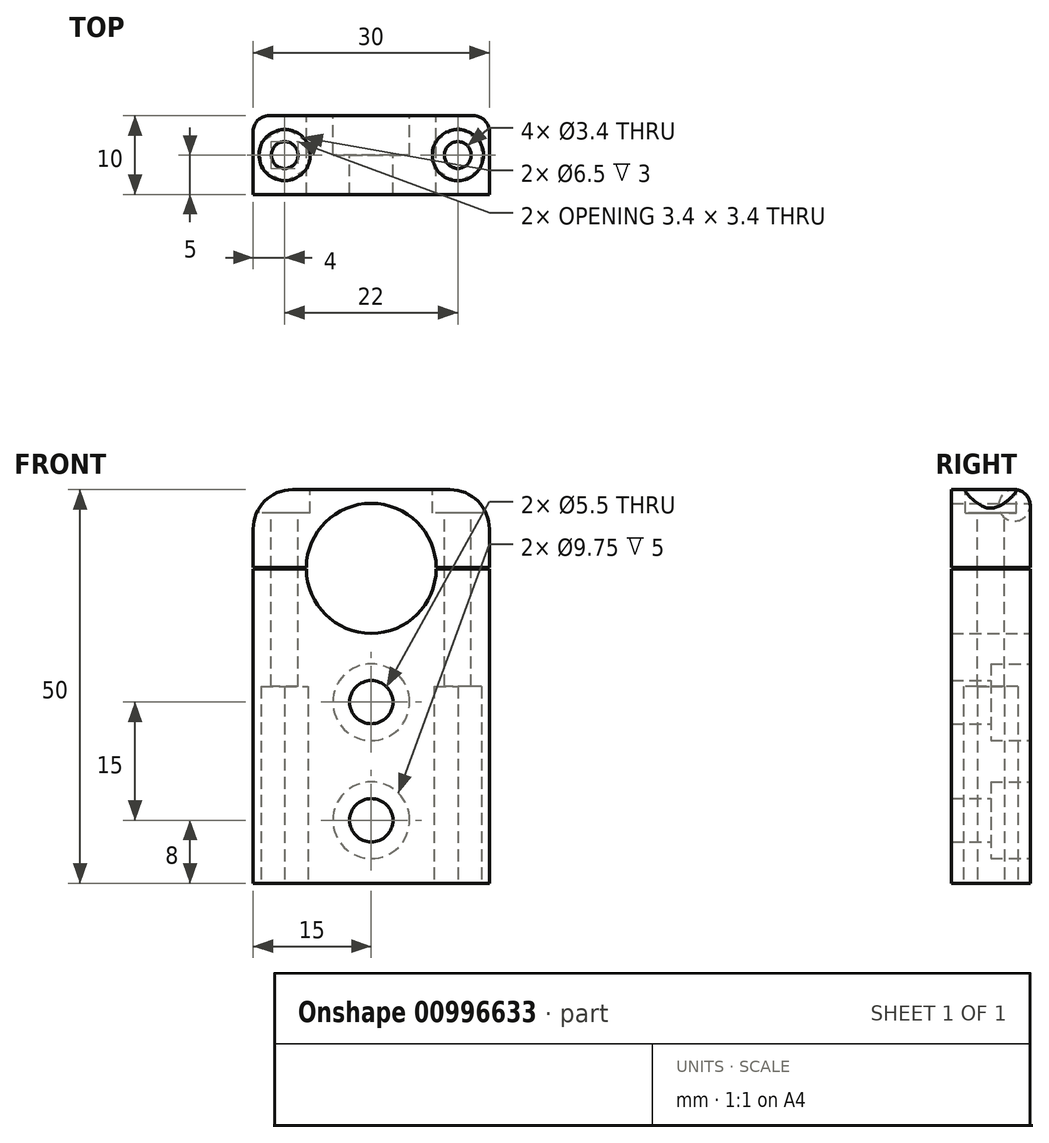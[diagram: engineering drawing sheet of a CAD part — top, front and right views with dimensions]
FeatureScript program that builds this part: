
annotation { "Feature Type Name" : "Feature", "Feature Type Description" : "" }
export const myFeature = defineFeature(function(context is Context, id is Id, definition is map)
    precondition{}
    {
        {
            var Q0;
            Q0=qCreatedBy(makeId("Front.planeOp"),FACE);
            var sketch = newSketch(context, id + "F0", { "sketchPlane" : qUnion([Q0])});
            skCircle(sketch, "E0", {"center": v(0, 0) * mm, "radius": 8.25 * mm});
            skLineSegment(sketch, "E1.bottom", {"start": v(-15, 10) * mm, "end": v(15, 10) * mm});
            skLineSegment(sketch, "E1.top", {"start": v(-15, -40) * mm, "end": v(15, -40) * mm});
            skLineSegment(sketch, "E1.left", {"start": v(-15, 10) * mm, "end": v(-15, -40) * mm});
            skLineSegment(sketch, "E1.right", {"start": v(15, 10) * mm, "end": v(15, -40) * mm});
            skPoint(sketch, "E1.middle", {"position": v(0, -15) * mm});
            skPoint(sketch, "E2", {"position": v(0, -32) * mm});
            skPoint(sketch, "E3", {"position": v(0, -17) * mm});
            skSolve(sketch);
        }
        {
            var Q0;
            Q0=makeQuery(id+"F0.imprint","IMPRINT",FACE,{"disambiguationData":[TD([[makeQuery(id+"F0.imprint","IMPRINT",EDGE,{"derivedFrom":sQuery(id+"F0.wireOp",EDGE,"E0")}),-1.0]])]});
            extrude(context, id + "F1", {"entities" : qUnion([Q0]), "depth" : 10 * mm, "offsetDistance" : 25 * mm});
        }
        {
            var Q0;
            Q0=sQuery(id+"F0.wireOp",VERTEX,"E3");
            var Q1;
            Q1=sQuery(id+"F0.wireOp",VERTEX,"E2");
            var Q2;
            Q2=makeQuery(id+"F1.opExtrude","SWEPT_BODY",BODY,{"disambiguationData":[OSD([sQuery(id+"F0.wireOp",EDGE,"E0"),sQuery(id+"F0.wireOp",EDGE,"E1.bottom"),sQuery(id+"F0.wireOp",EDGE,"E1.top"),sQuery(id+"F0.wireOp",EDGE,"E1.left"),sQuery(id+"F0.wireOp",EDGE,"E1.right")])]});
            hole(context, id + "F2", {"style" : HoleStyle.C_BORE, "endStyle" : HoleEndStyle.THROUGH, "oppositeDirection" : true, "standardTappedOrClearance" : lookupTablePath({ "fit" : "Normal", "standard" : "ISO", "size" : "M5", "type" : "Clearance" }), "standardBlindInLast" : lookupTablePath({ "fit" : "Normal", "standard" : "ISO", "engagement" : "75%", "pitch" : "0.8 mm", "size" : "M5", "type" : "Clearance & tapped" }), "holeDiameter" : 5.5 * mm, "cBoreDiameter" : 9.75 * mm, "cBoreDepth" : 5 * mm, "majorDiameter" : 5 * mm, "isTappedThrough" : true, "tappedDepth" : 12 * mm, "tapClearance" : 3, "locations" : qUnion([Q0, Q1]), "scope" : qUnion([Q2])});
        }
        {
            var Q0;
            Q0=makeQuery(id+"F1.opExtrude","SWEPT_FACE",FACE,{"disambiguationData":[OSD([sQuery(id+"F0.wireOp",EDGE,"E1.bottom")])]});
            var sketch = newSketch(context, id + "F3", { "sketchPlane" : qUnion([Q0])});
            skPoint(sketch, "E4", {"position": v(-11, -5) * mm});
            skPoint(sketch, "E4.positionSnap0", {"position": v(-15, -5) * mm});
            skPoint(sketch, "E5", {"position": v(11, -5) * mm});
            skSolve(sketch);
        }
        {
            var Q0;
            Q0=sQuery(id+"F3.wireOp",VERTEX,"E5");
            var Q1;
            Q1=sQuery(id+"F3.wireOp",VERTEX,"E4");
            var Q2;
            Q2=makeQuery(id+"F1.opExtrude","SWEPT_BODY",BODY,{"disambiguationData":[OSD([sQuery(id+"F0.wireOp",EDGE,"E0"),sQuery(id+"F0.wireOp",EDGE,"E1.bottom"),sQuery(id+"F0.wireOp",EDGE,"E1.top"),sQuery(id+"F0.wireOp",EDGE,"E1.left"),sQuery(id+"F0.wireOp",EDGE,"E1.right")])]});
            hole(context, id + "F4", {"style" : HoleStyle.C_BORE, "endStyle" : HoleEndStyle.THROUGH, "standardTappedOrClearance" : lookupTablePath({ "fit" : "Normal", "standard" : "ISO", "size" : "M3", "type" : "Clearance" }), "standardBlindInLast" : lookupTablePath({ "fit" : "Normal", "standard" : "ISO", "engagement" : "75%", "pitch" : "0.5 mm", "size" : "M3", "type" : "Clearance & tapped" }), "holeDiameter" : 3.4 * mm, "cBoreDiameter" : 6.5 * mm, "cBoreDepth" : 3 * mm, "majorDiameter" : 5 * mm, "isTappedThrough" : true, "tappedDepth" : 12 * mm, "tapClearance" : 3, "locations" : qUnion([Q0, Q1]), "scope" : qUnion([Q2])});
        }
        {
            var Q0;
            Q0=makeQuery(id+"F1.opExtrude","SWEPT_EDGE",EDGE,{"disambiguationData":[OSD([sQuery(id+"F0.wireOp",EDGE,"E1.bottom"),sQuery(id+"F0.wireOp",EDGE,"E1.right")])]});
            var Q1;
            Q1=makeQuery(id+"F1.opExtrude","SWEPT_EDGE",EDGE,{"disambiguationData":[OSD([sQuery(id+"F0.wireOp",EDGE,"E1.bottom"),sQuery(id+"F0.wireOp",EDGE,"E1.left")])]});
            fillet(context, id + "F5", {"entities" : qUnion([Q0, Q1]), "radius" : 5 * mm, "tangentPropagation" : true, "allowEdgeOverflow" : false});
        }
        {
            var Q0;
            Q0=makeQuery(id+"F1.opExtrude","SWEPT_FACE",FACE,{"disambiguationData":[OSD([sQuery(id+"F0.wireOp",EDGE,"E1.top")])]});
            var sketch = newSketch(context, id + "F6", { "sketchPlane" : qUnion([Q0])});
            skCircle(sketch, "E6.cCircle", {"center": v(11, 5) * mm, "radius": 3 * mm, "construction": true});
            skLineSegment(sketch, "E6.0", {"start": v(8, 6.73) * mm, "end": v(11, 8.46) * mm});
            skLineSegment(sketch, "E6.1", {"start": v(11, 8.46) * mm, "end": v(14, 6.73) * mm});
            skLineSegment(sketch, "E6.2", {"start": v(14, 6.73) * mm, "end": v(14, 3.27) * mm});
            skLineSegment(sketch, "E6.3", {"start": v(14, 3.27) * mm, "end": v(11, 1.54) * mm});
            skLineSegment(sketch, "E6.4", {"start": v(11, 1.54) * mm, "end": v(8, 3.27) * mm});
            skLineSegment(sketch, "E6.5", {"start": v(8, 3.27) * mm, "end": v(8, 6.73) * mm});
            skPoint(sketch, "E6.0.midPoint", {"position": v(9.5, 7.6) * mm});
            skLineSegment(sketch, "E7.MirrorCS", {"start": v(-11, 8.46) * mm, "end": v(-14, 6.73) * mm});
            skLineSegment(sketch, "E8.MirrorCS", {"start": v(-8, 6.73) * mm, "end": v(-11, 8.46) * mm});
            skLineSegment(sketch, "E9.MirrorCS", {"start": v(-11, 1.54) * mm, "end": v(-8, 3.27) * mm});
            skLineSegment(sketch, "E10.MirrorCS", {"start": v(-14, 3.27) * mm, "end": v(-11, 1.54) * mm});
            skLineSegment(sketch, "E11.MirrorCS", {"start": v(-14, 6.73) * mm, "end": v(-14, 3.27) * mm});
            skPoint(sketch, "E12.MirrorP", {"position": v(-9.5, 7.6) * mm});
            skLineSegment(sketch, "E13.MirrorCS", {"start": v(-8, 3.27) * mm, "end": v(-8, 6.73) * mm});
            skCircle(sketch, "E14.MirrorC", {"center": v(-11, 5) * mm, "radius": 3 * mm, "construction": true});
            skSolve(sketch);
        }
        {
            var Q0;
            Q0=makeQuery(id+"F6.imprint","IMPRINT",FACE,{"disambiguationData":[TD([[makeQuery(id+"F6.imprint","IMPRINT",EDGE,{"derivedFrom":sQuery(id+"F6.wireOp",EDGE,"E6.0")}),-1.0]])]});
            var Q1;
            Q1=makeQuery(id+"F6.imprint","IMPRINT",FACE,{"disambiguationData":[TD([[makeQuery(id+"F6.imprint","IMPRINT",EDGE,{"derivedFrom":sQuery(id+"F6.wireOp",EDGE,"E7.MirrorCS")}),1.0]])]});
            extrude(context, id + "F7", {"entities" : qUnion([Q0, Q1]), "operationType" : NewBodyOperationType.REMOVE, "oppositeDirection" : true, "depth" : 25 * mm, "offsetDistance" : 25 * mm});
        }
        {
            var Q0;
            Q0=makeQuery(id+"F1.opExtrude","CAP_EDGE",EDGE,{"disambiguationData":[OSD([sQuery(id+"F0.wireOp",EDGE,"E1.right")])],"isStart":true});
            fillet(context, id + "F8", {"entities" : qUnion([Q0]), "radius" : 2 * mm, "tangentPropagation" : true, "allowEdgeOverflow" : false});
        }
        {
            var Q0;
            Q0=makeQuery(id+"F0.imprint","IMPRINT",FACE,{"disambiguationData":[TD([[makeQuery(id+"F0.imprint","IMPRINT",EDGE,{"derivedFrom":sQuery(id+"F0.wireOp",EDGE,"E0")}),-1.0]])]});
            var sketch = newSketch(context, id + "F9", { "sketchPlane" : qUnion([Q0])});
            skLineSegment(sketch, "E15.bottom", {"start": v(25, 0.1) * mm, "end": v(-25, 0.1) * mm});
            skLineSegment(sketch, "E15.top", {"start": v(25, -0.1) * mm, "end": v(-25, -0.1) * mm});
            skLineSegment(sketch, "E15.left", {"start": v(25, 0.1) * mm, "end": v(25, -0.1) * mm});
            skLineSegment(sketch, "E15.right", {"start": v(-25, 0.1) * mm, "end": v(-25, -0.1) * mm});
            skPoint(sketch, "E15.middle", {"position": v(0, 0) * mm});
            skSolve(sketch);
        }
        {
            var Q0;
            Q0 = qSketchRegion(id + "F9", true);
            extrude(context, id + "F10", {"entities" : qUnion([Q0]), "operationType" : NewBodyOperationType.REMOVE, "depth" : 25 * mm, "offsetDistance" : 25 * mm});
        }
    });
